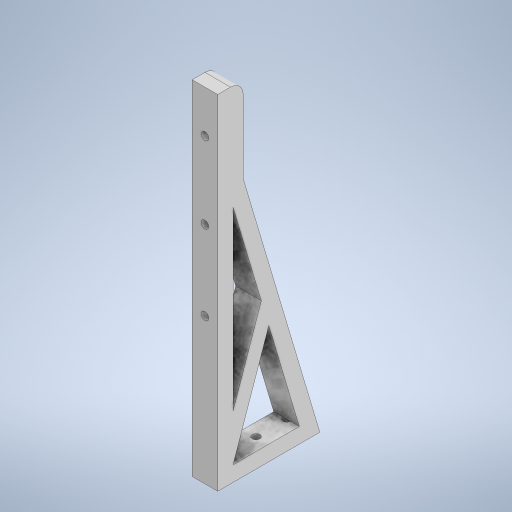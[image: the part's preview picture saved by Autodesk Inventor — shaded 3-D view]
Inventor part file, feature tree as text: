
AUTODESK INVENTOR PART (.ipt)
format: ipt  version: 2023 (Build 270158000, 158)  size: 376,832 bytes
history: native  units: mm
features: extrude x8, sketch x8, other x2, fillet x1
ambient origin geometry x8: Origin, YZ Plane, XZ Plane, XY Plane, X Axis, Y Axis, Z Axis, Center Point
bodies: Body1 (feature_tree)
feature tree (19):
  other  "솔리드1"
  extrude  "돌출1"  Depth=66.0mm
  extrude  "돌출2"  Depth=10.0mm
  other  "작업 평면1"
  extrude  "돌출3"  Depth=10.0mm
  extrude  "돌출4"  Depth=30.0mm
  extrude  "돌출5"  Depth=50.0mm TaperAngle=0.0deg
  extrude  "돌출6"  Depth=28.0mm
  extrude  "돌출7"  Depth=150.0mm
  fillet  "모깎기2"  Radius=10.0mm
  extrude  "돌출8"  Depth=16.0mm
  sketch  "스케치1"
  sketch  "스케치2"
  sketch  "스케치3"
  sketch  "스케치4"
  sketch  "스케치5"
  sketch  "스케치6"
  sketch  "스케치7"
  sketch  "스케치8"
